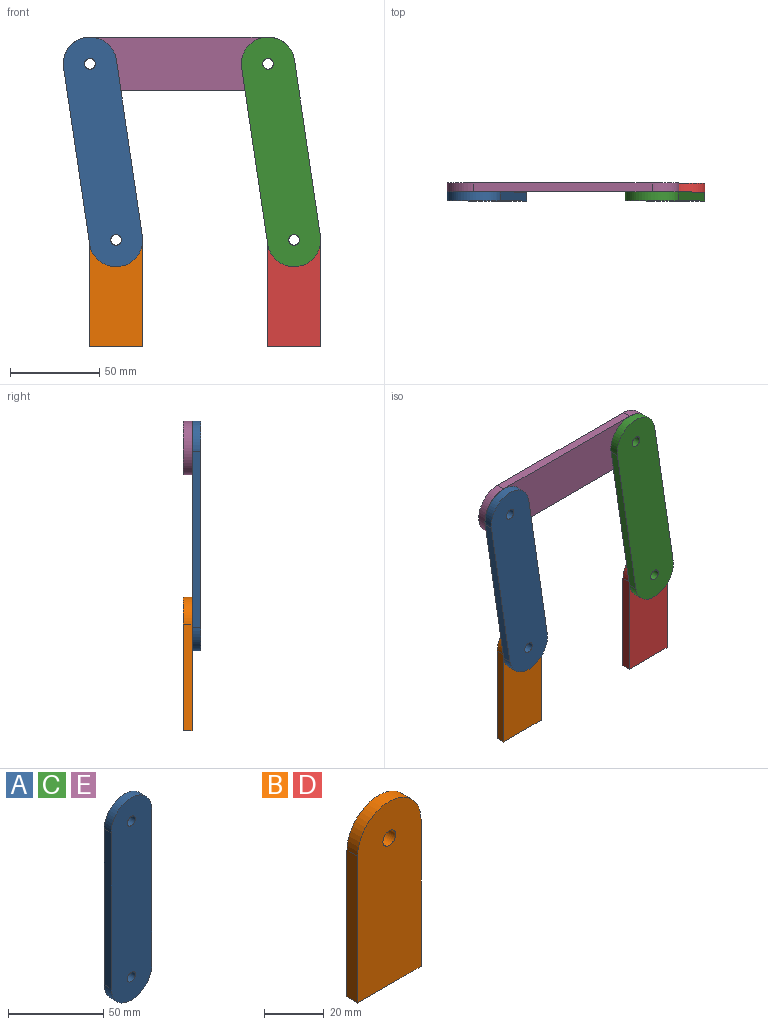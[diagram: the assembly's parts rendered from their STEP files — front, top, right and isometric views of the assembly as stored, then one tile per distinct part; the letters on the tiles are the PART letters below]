
ASSEMBLY  parts=5 mates=5
PART A: 8 faces, bbox 30x5x130 mm
  f0: plane 100x5mm, normal (1,0,0), area 500mm2, adj f1,f5,f6,f7
  f1: cylinder r=15mm len=30mm, axis (0,1,0), area 235.6mm2, adj f0,f2,f6,f7
  f2: plane 100x5mm, normal (-1,0,0), area 500mm2, adj f1,f5,f6,f7
  f3: cylinder r=3mm len=6mm, axis (0,1,0), area 94.2mm2, adj f6,f7
  f4: cylinder r=3mm len=6mm, axis (0,1,0), area 94.2mm2, adj f6,f7
  f5: cylinder r=15mm len=30mm, axis (0,1,0), area 235.6mm2, adj f0,f2,f6,f7
  f6: plane 130x30mm, normal (0,-1,0), area 3650.3mm2, adj f0,f1,f2,f3,f4,f5
  f7: plane 130x30mm, normal (0,1,0), area 3650.3mm2, adj f0,f1,f2,f3,f4,f5
PART B: 7 faces, bbox 30x5x75 mm
  f0: plane 30x5mm, normal (0,0,-1), area 150mm2, adj f1,f3,f5,f6
  f1: plane 60x5mm, normal (1,0,0), area 300mm2, adj f0,f2,f5,f6
  f2: cylinder r=15mm len=30mm, axis (0,1,0), area 235.6mm2, adj f1,f3,f5,f6
  f3: plane 60x5mm, normal (-1,0,0), area 300mm2, adj f0,f2,f5,f6
  f4: cylinder r=3mm len=6mm, axis (0,1,0), area 94.2mm2, adj f5,f6
  f5: plane 75x30mm, normal (0,-1,0), area 2125.2mm2, adj f0,f1,f2,f3,f4
  f6: plane 75x30mm, normal (0,1,0), area 2125.2mm2, adj f0,f1,f2,f3,f4
PART C: same geometry as A
PART D: same geometry as B
PART E: same geometry as A
PLACE A rot(axis=(0,-1,0),8.4deg) t=(-28.22,0,250.94)mm
PLACE B t=(0,5,30)mm
PLACE C rot(axis=(0,-1,0),8.4deg) t=(71.78,0,250.94)mm
PLACE D t=(100,5,30)mm
PLACE E rot(axis=(0,-1,0),90deg) t=(-107.64,5,158.93)mm
MATE fastened D.f5 <-> B.f5  axis (0,-1,0) through (100,0,0)mm
MATE revolute E.f4 <-> C.f1  axis (0,-1,0) through (85.38,0,158.93)mm
MATE revolute C.f4 <-> D.f4  axis (0,1,0) through (100,0,60)mm
MATE revolute A.f4 <-> B.f4  axis (0,1,0) through (0,0,60)mm
MATE revolute E.f1 <-> A.f1  axis (0,-1,0) through (-14.62,0,158.93)mm
